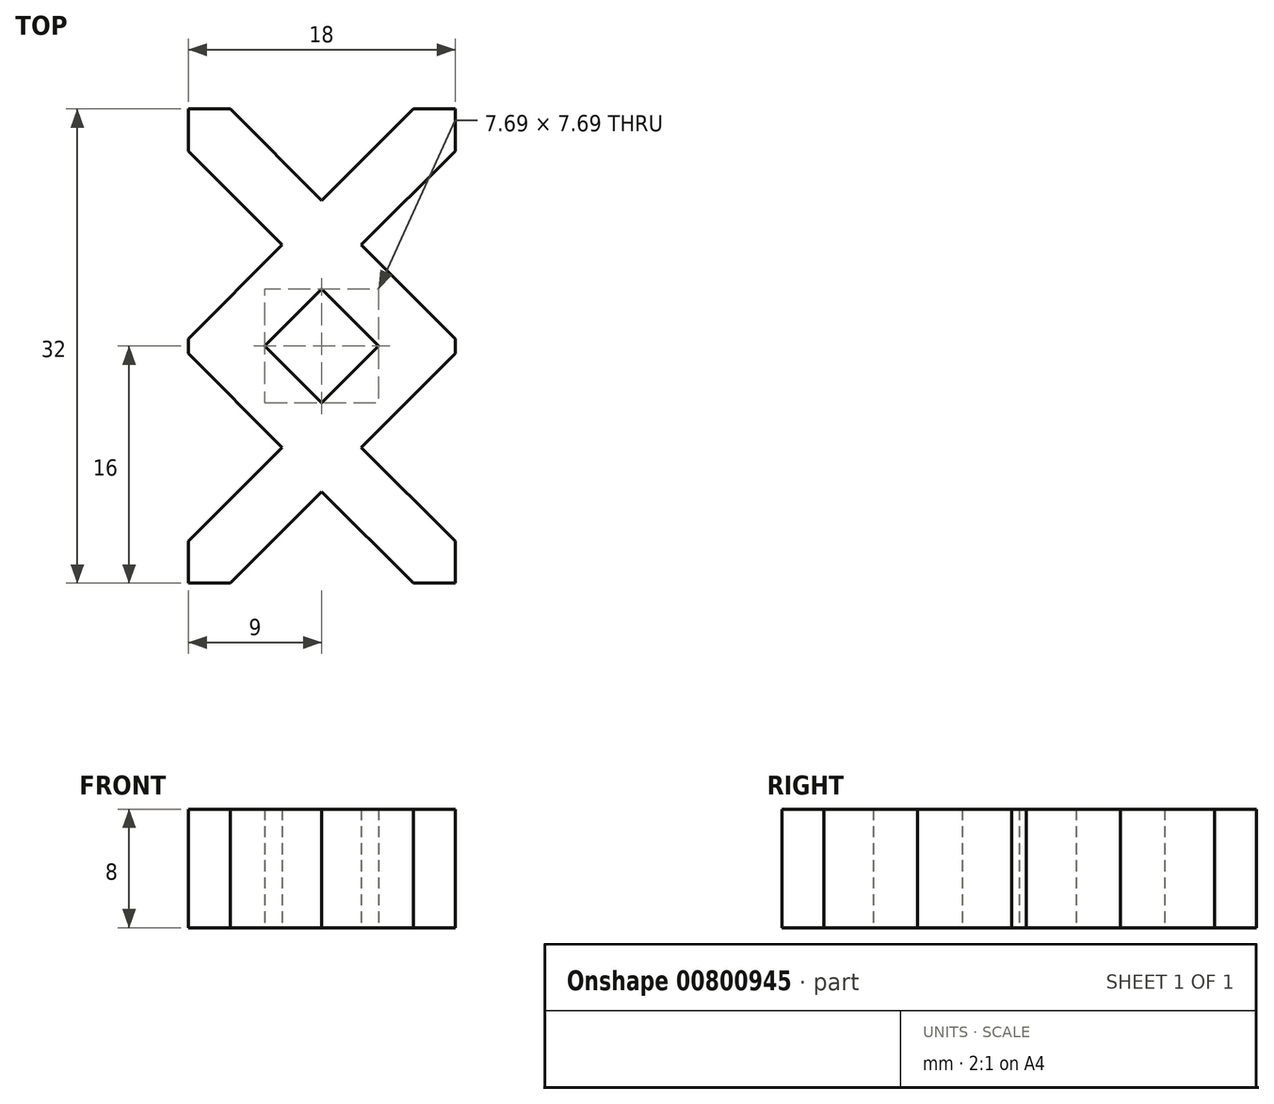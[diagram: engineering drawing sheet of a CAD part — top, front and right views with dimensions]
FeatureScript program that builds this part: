
annotation { "Feature Type Name" : "Feature", "Feature Type Description" : "" }
export const myFeature = defineFeature(function(context is Context, id is Id, definition is map)
    precondition{}
    {
        {
            var Q0;
            Q0=qCreatedBy(makeId("Top.planeOp"),FACE);
            var sketch = newSketch(context, id + "F0", { "sketchPlane" : qUnion([Q0])});
            skLineSegment(sketch, "E0", {"start": v(0, 0) * mm, "end": v(2.83, 0) * mm});
            skLineSegment(sketch, "E1", {"start": v(2.83, 0) * mm, "end": v(9, -6.17) * mm});
            skLineSegment(sketch, "E2", {"start": v(9, -6.17) * mm, "end": v(15.17, 0) * mm});
            skLineSegment(sketch, "E3", {"start": v(15.17, 0) * mm, "end": v(18, 0) * mm});
            skLineSegment(sketch, "E4", {"start": v(18, 0) * mm, "end": v(18, -2.83) * mm});
            skLineSegment(sketch, "E5", {"start": v(18, -2.83) * mm, "end": v(11.66, -9.16) * mm});
            skLineSegment(sketch, "E6", {"start": v(11.66, -22.84) * mm, "end": v(18, -29.17) * mm});
            skLineSegment(sketch, "E7", {"start": v(18, -29.17) * mm, "end": v(18, -32) * mm});
            skLineSegment(sketch, "E8", {"start": v(18, -32) * mm, "end": v(15.17, -32) * mm});
            skLineSegment(sketch, "E9", {"start": v(15.17, -32) * mm, "end": v(9, -25.83) * mm});
            skLineSegment(sketch, "E10", {"start": v(9, -25.83) * mm, "end": v(2.83, -32) * mm});
            skLineSegment(sketch, "E11", {"start": v(2.83, -32) * mm, "end": v(0, -32) * mm});
            skLineSegment(sketch, "E12", {"start": v(0, -32) * mm, "end": v(0, -29.17) * mm});
            skLineSegment(sketch, "E13", {"start": v(0, -29.17) * mm, "end": v(6.34, -22.84) * mm});
            skLineSegment(sketch, "E14", {"start": v(6.34, -22.84) * mm, "end": v(0, -16.5) * mm});
            skLineSegment(sketch, "E15", {"start": v(0, -16.5) * mm, "end": v(0, -15.5) * mm});
            skLineSegment(sketch, "E16", {"start": v(0, -15.5) * mm, "end": v(6.34, -9.16) * mm});
            skLineSegment(sketch, "E17", {"start": v(6.34, -9.16) * mm, "end": v(0, -2.83) * mm});
            skLineSegment(sketch, "E18", {"start": v(0, -2.83) * mm, "end": v(0, 0) * mm});
            skLineSegment(sketch, "E19", {"start": v(11.66, -9.16) * mm, "end": v(18, -15.5) * mm});
            skLineSegment(sketch, "E20", {"start": v(18, -15.5) * mm, "end": v(18, -16.5) * mm});
            skLineSegment(sketch, "E21", {"start": v(18, -16.5) * mm, "end": v(11.66, -22.84) * mm});
            skLineSegment(sketch, "E22", {"start": v(9, -12.16) * mm, "end": v(5.16, -16) * mm});
            skLineSegment(sketch, "E23", {"start": v(5.16, -16) * mm, "end": v(9, -19.84) * mm});
            skLineSegment(sketch, "E24", {"start": v(9, -19.84) * mm, "end": v(12.84, -16) * mm});
            skLineSegment(sketch, "E25", {"start": v(12.84, -16) * mm, "end": v(9, -12.16) * mm});
            skSolve(sketch);
        }
        {
            var Q0;
            Q0=makeQuery(id+"F0.imprint","IMPRINT",FACE,{"disambiguationData":[TD([[makeQuery(id+"F0.imprint","IMPRINT",EDGE,{"derivedFrom":sQuery(id+"F0.wireOp",EDGE,"E0")}),-1.0]])]});
            extrude(context, id + "F1", {"entities" : qUnion([Q0]), "depth" : 8 * mm, "offsetDistance" : 25 * mm});
        }
    });
